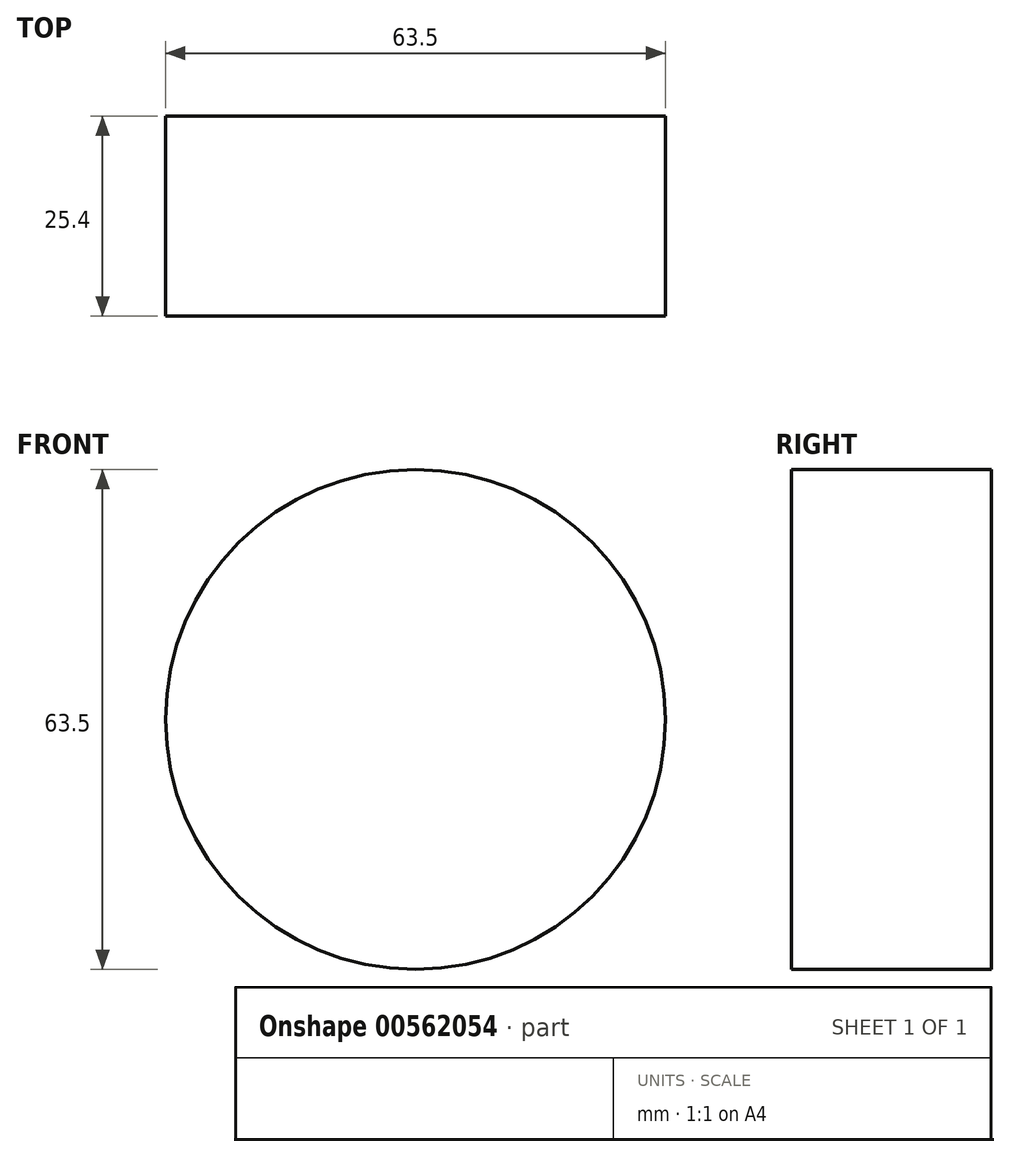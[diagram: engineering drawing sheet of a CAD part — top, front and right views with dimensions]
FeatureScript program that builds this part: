
annotation { "Feature Type Name" : "Feature", "Feature Type Description" : "" }
export const myFeature = defineFeature(function(context is Context, id is Id, definition is map)
    precondition{}
    {
        {
            var Q0;
            Q0=qCreatedBy(makeId("Front.planeOp"),FACE);
            var sketch = newSketch(context, id + "F0", { "sketchPlane" : qUnion([Q0])});
            skCircle(sketch, "E0", {"center": v(-17.78, 50.8) * mm, "radius": 31.75 * mm});
            skSolve(sketch);
        }
        {
            var Q0;
            Q0=makeQuery(id+"F0.imprint","IMPRINT",FACE,{"disambiguationData":[TD([[makeQuery(id+"F0.imprint","IMPRINT",EDGE,{"derivedFrom":sQuery(id+"F0.wireOp",EDGE,"E0")}),1.0]])]});
            extrude(context, id + "F1", {"entities" : qUnion([Q0]), "depth" : 25.4 * mm, "offsetDistance" : 25.4 * mm});
        }
    });
